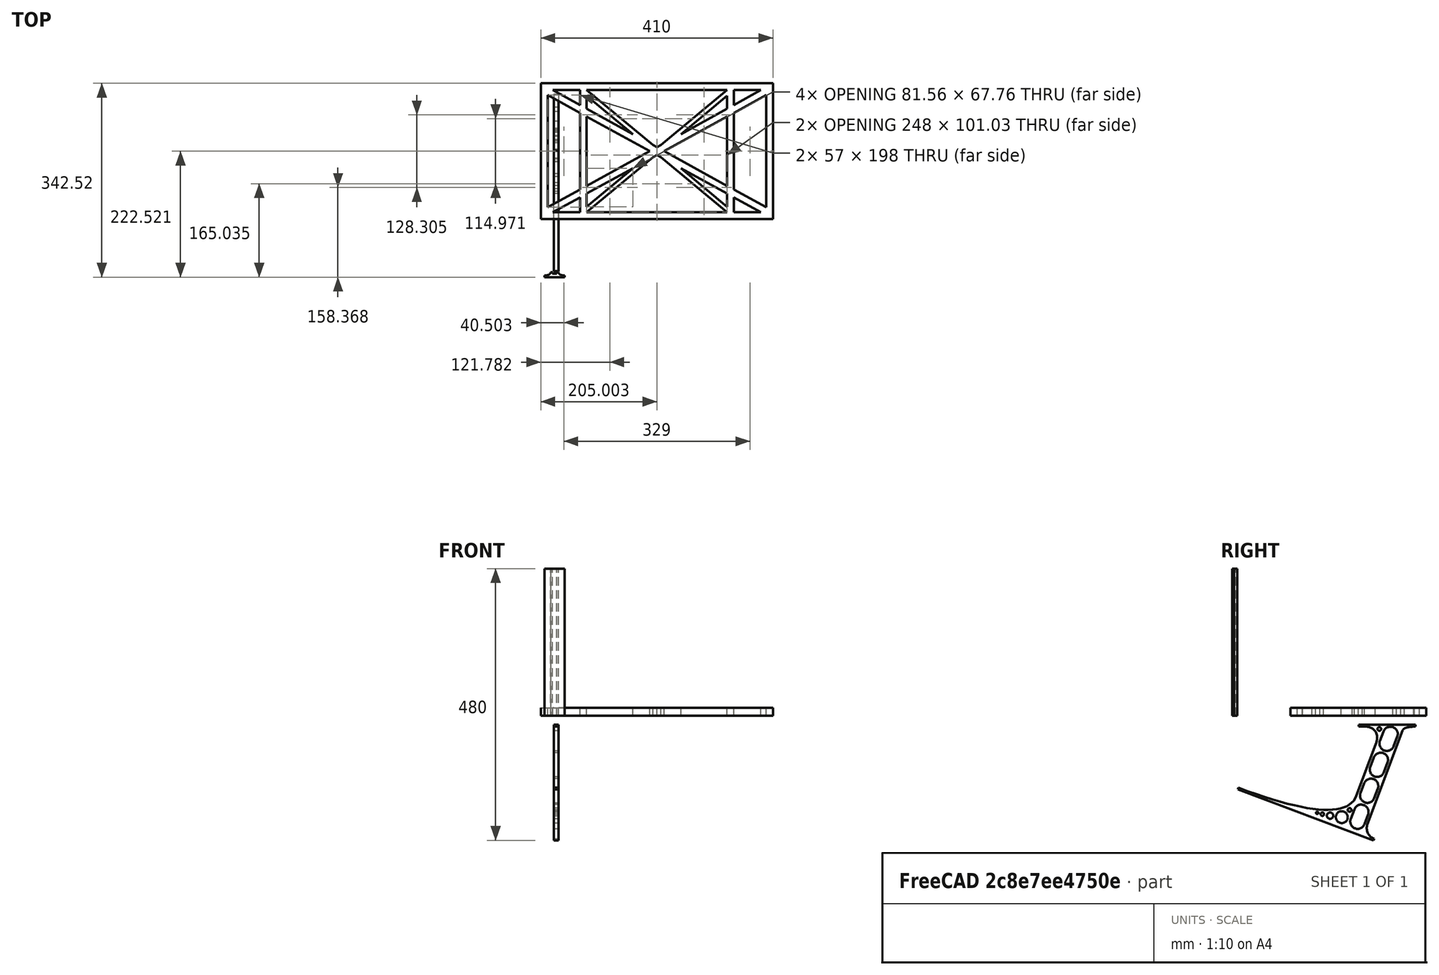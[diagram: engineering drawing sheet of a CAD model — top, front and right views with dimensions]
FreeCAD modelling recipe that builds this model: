
FCSTD DOCUMENT  (FreeCAD 0.19R0.19.2)
Label: laptopStand057
License: All rights reserved
LicenseURL: http://en.wikipedia.org/wiki/All_rights_reserved
objects: Sketcher::SketchObject×3, Part::Extrusion×3
note: 6 computed .brp shape members not serialized (recipe doc carries the construction recipe); baked Part::Feature solids carry a one-line shape summary decoded from their .brp

FEATURE [Sketcher::SketchObject] Sketch
  FullyConstrained = false
  sketch-geometry (106):
    g0: LineSegment StartX=-22.9272 StartY=136.221 StartZ=0 EndX=387.073 EndY=136.221 EndZ=0
    g1: LineSegment StartX=-22.9272 StartY=-103.779 StartZ=0 EndX=387.073 EndY=-103.779 EndZ=0
    g2: LineSegment StartX=375.073 StartY=115.221 StartZ=0 EndX=318.073 EndY=83.9235 EndZ=0
    g3: LineSegment StartX=-10.9272 StartY=-82.7794 StartZ=0 EndX=46.0728 EndY=-51.4823 EndZ=0
    g4: LineSegment StartX=-1.92718 StartY=124.221 StartZ=0 EndX=46.0728 EndY=97.8651 EndZ=0
    g5: LineSegment StartX=366.073 StartY=-91.7794 StartZ=0 EndX=318.073 EndY=-65.424 EndZ=0
    g6: LineSegment StartX=-10.9272 StartY=115.221 StartZ=0 EndX=-10.9272 EndY=-82.7794 EndZ=0
    g7: LineSegment StartX=375.073 StartY=-82.7794 StartZ=0 EndX=375.073 EndY=115.221 EndZ=0
    g8: LineSegment StartX=-1.92719 StartY=-91.7794 StartZ=0 EndX=46.0728 EndY=-91.7794 EndZ=0
    g9: LineSegment StartX=318.073 StartY=124.221 StartZ=0 EndX=366.073 EndY=124.221 EndZ=0
    g10: LineSegment StartX=306.073 StartY=-81.8102 StartZ=0 EndX=224.513 EndY=-14.0532 EndZ=0
    g11: LineSegment StartX=58.0728 StartY=114.251 StartZ=0 EndX=139.632 EndY=46.4944 EndZ=0
    g12: LineSegment StartX=306.073 StartY=124.221 StartZ=0 EndX=189.124 EndY=27.0628 EndZ=0
    g13: LineSegment StartX=58.0728 StartY=-91.7794 StartZ=0 EndX=175.022 EndY=5.37834 EndZ=0
    g14: LineSegment StartX=46.0728 StartY=124.221 StartZ=0 EndX=46.0728 EndY=97.8651 EndZ=0
    g15: LineSegment StartX=58.0728 StartY=-81.8102 StartZ=0 EndX=58.0728 EndY=-58.8351 EndZ=0
    g16: LineSegment StartX=318.073 StartY=124.221 StartZ=0 EndX=318.073 EndY=97.8651 EndZ=0
    g17: LineSegment StartX=306.073 StartY=114.251 StartZ=0 EndX=306.073 EndY=91.2763 EndZ=0
    g18: LineSegment StartX=224.513 StartY=46.4944 StartZ=0 EndX=306.073 EndY=114.251 EndZ=0
    g19: LineSegment StartX=175.022 StartY=27.0628 StartZ=0 EndX=58.0728 EndY=124.221 EndZ=0
    g20: LineSegment StartX=169.377 StartY=16.2206 StartZ=0 EndX=58.0728 EndY=77.3346 EndZ=0
    g21: LineSegment StartX=139.632 StartY=-14.0532 StartZ=0 EndX=58.0728 EndY=-81.8102 EndZ=0
    g22: LineSegment StartX=194.768 StartY=16.2206 StartZ=0 EndX=306.073 EndY=-44.8935 EndZ=0
    g23: LineSegment StartX=224.513 StartY=46.4944 StartZ=0 EndX=306.073 EndY=91.2763 EndZ=0
    g24: LineSegment StartX=139.632 StartY=-14.0532 StartZ=0 EndX=58.0728 EndY=-58.8351 EndZ=0
    g25: LineSegment StartX=189.124 StartY=5.37834 StartZ=0 EndX=306.073 EndY=-91.7794 EndZ=0
    g26: LineSegment StartX=306.073 StartY=77.3346 StartZ=0 EndX=306.073 EndY=-44.8935 EndZ=0
    g27: LineSegment StartX=318.073 StartY=83.9235 StartZ=0 EndX=318.073 EndY=-51.4823 EndZ=0
    g28: LineSegment StartX=318.073 StartY=97.8651 StartZ=0 EndX=366.073 EndY=124.221 EndZ=0
    g29: LineSegment StartX=306.073 StartY=77.3346 StartZ=0 EndX=194.768 EndY=16.2206 EndZ=0
    g30: LineSegment StartX=306.073 StartY=-58.8351 StartZ=0 EndX=224.513 EndY=-14.0532 EndZ=0
    g31: LineSegment StartX=306.073 StartY=-58.8351 StartZ=0 EndX=306.073 EndY=-81.8102 EndZ=0
    g32: LineSegment StartX=318.073 StartY=-51.4823 StartZ=0 EndX=375.073 EndY=-82.7794 EndZ=0
    g33: LineSegment StartX=318.073 StartY=-65.424 StartZ=0 EndX=318.073 EndY=-91.7794 EndZ=0
    g34: LineSegment StartX=318.073 StartY=-91.7794 StartZ=0 EndX=366.073 EndY=-91.7794 EndZ=0
    g35: LineSegment StartX=58.0728 StartY=-44.8935 StartZ=0 EndX=58.0728 EndY=77.3346 EndZ=0
    g36: LineSegment StartX=46.0728 StartY=-65.424 StartZ=0 EndX=-1.92719 EndY=-91.7794 EndZ=0
    g37: LineSegment StartX=46.0728 StartY=-65.424 StartZ=0 EndX=46.0728 EndY=-91.7794 EndZ=0
    g38: LineSegment StartX=58.0728 StartY=-44.8935 StartZ=0 EndX=169.377 EndY=16.2206 EndZ=0
    g39: LineSegment StartX=58.0728 StartY=91.2763 StartZ=0 EndX=58.0728 EndY=114.251 EndZ=0
    g40: LineSegment StartX=46.0728 StartY=83.9235 StartZ=0 EndX=46.0728 EndY=-51.4823 EndZ=0
    g41: LineSegment StartX=46.0728 StartY=124.221 StartZ=0 EndX=-1.92719 EndY=124.221 EndZ=0
    g42: LineSegment StartX=58.0728 StartY=91.2763 StartZ=0 EndX=139.632 EndY=46.4944 EndZ=0
    g43: LineSegment StartX=46.0728 StartY=83.9235 StartZ=0 EndX=-10.9272 EndY=115.221 EndZ=0
    g44: LineSegment StartX=-22.9272 StartY=136.221 StartZ=0 EndX=-42.9272 EndY=136.221 EndZ=0
    g45: LineSegment StartX=387.073 StartY=136.221 StartZ=0 EndX=407.073 EndY=136.221 EndZ=0
    g46: LineSegment StartX=-42.9272 StartY=136.221 StartZ=0 EndX=-42.9272 EndY=-103.779 EndZ=0
    g47: LineSegment StartX=-22.9272 StartY=-103.779 StartZ=0 EndX=-42.9272 EndY=-103.779 EndZ=0
    g48: LineSegment StartX=407.073 StartY=136.221 StartZ=0 EndX=407.073 EndY=-103.779 EndZ=0
    g49: LineSegment StartX=387.073 StartY=-103.779 StartZ=0 EndX=407.073 EndY=-103.779 EndZ=0
    g50: LineSegment StartX=179.022 StartY=27.0628 StartZ=0 EndX=179.022 EndY=124.221 EndZ=0
    g51: LineSegment StartX=185.124 StartY=27.0628 StartZ=0 EndX=185.124 EndY=124.221 EndZ=0
    g52: ArcOfCircle CenterX=-26.9272 CenterY=22.1087 CenterZ=0 NormalX=0 NormalY=0 NormalZ=1 AngleXU=0 Radius=8 StartAngle=1e-16 EndAngle=3.14159
    g53: ArcOfCircle CenterX=-26.9272 CenterY=-83.7794 CenterZ=0 NormalX=0 NormalY=0 NormalZ=1 AngleXU=0 Radius=8 StartAngle=3.14159 EndAngle=6.28319
    g54: LineSegment StartX=-34.9272 StartY=22.1087 StartZ=0 EndX=-34.9272 EndY=-83.7794 EndZ=0
    g55: LineSegment StartX=-18.9272 StartY=22.1087 StartZ=0 EndX=-18.9272 EndY=-83.7794 EndZ=0
    g56: LineSegment StartX=185.124 StartY=-91.7794 StartZ=0 EndX=306.073 EndY=-91.7794 EndZ=0
    g57: LineSegment StartX=179.022 StartY=-91.7794 StartZ=0 EndX=58.0728 EndY=-91.7794 EndZ=0
    g58: LineSegment StartX=306.073 StartY=124.221 StartZ=0 EndX=185.124 EndY=124.221 EndZ=0
    g59: LineSegment StartX=179.022 StartY=124.221 StartZ=0 EndX=58.0728 EndY=124.221 EndZ=0
    g60: ArcOfCircle CenterX=391.073 CenterY=22.1087 CenterZ=0 NormalX=0 NormalY=0 NormalZ=1 AngleXU=0 Radius=8 StartAngle=-4.4e-15 EndAngle=3.14159
    g61: LineSegment StartX=399.073 StartY=22.1087 StartZ=0 EndX=399.073 EndY=-83.7794 EndZ=0
    g62: LineSegment StartX=383.073 StartY=22.1087 StartZ=0 EndX=383.073 EndY=-83.7794 EndZ=0
    g63: ArcOfCircle CenterX=391.073 CenterY=-83.7794 CenterZ=0 NormalX=0 NormalY=0 NormalZ=1 AngleXU=0 Radius=8 StartAngle=3.14159 EndAngle=6.28319
    g64: Circle CenterX=175.022 CenterY=27.0628 CenterZ=0 NormalX=0 NormalY=0 NormalZ=1 AngleXU=0 Radius=1
    g65: Circle CenterX=179.022 CenterY=24.8665 CenterZ=0 NormalX=0 NormalY=0 NormalZ=1 AngleXU=0 Radius=1
    g66: Circle CenterX=179.022 CenterY=27.0628 CenterZ=0 NormalX=0 NormalY=0 NormalZ=1 AngleXU=0 Radius=1
    g67: BSplineCurve PolesCount=3 KnotsCount=2 Degree=2 IsPeriodic=0
    g68: GeomPoint X=175.022 Y=27.0628 Z=0
    g69: GeomPoint X=179.022 Y=27.0628 Z=0
    g70: Circle CenterX=189.124 CenterY=27.0628 CenterZ=0 NormalX=0 NormalY=0 NormalZ=1 AngleXU=0 Radius=1
    g71: Circle CenterX=185.124 CenterY=24.8665 CenterZ=0 NormalX=0 NormalY=0 NormalZ=1 AngleXU=0 Radius=1
    g72: Circle CenterX=185.124 CenterY=27.0628 CenterZ=0 NormalX=0 NormalY=0 NormalZ=1 AngleXU=0 Radius=1
    g73: BSplineCurve PolesCount=3 KnotsCount=2 Degree=2 IsPeriodic=0
    g74: GeomPoint X=189.124 Y=27.0628 Z=0
    g75: GeomPoint X=185.124 Y=27.0628 Z=0
    g76: Circle CenterX=175.022 CenterY=5.37834 CenterZ=0 NormalX=0 NormalY=0 NormalZ=1 AngleXU=0 Radius=1
    g77: Circle CenterX=179.022 CenterY=7.57463 CenterZ=0 NormalX=0 NormalY=0 NormalZ=1 AngleXU=0 Radius=1
    g78: Circle CenterX=179.022 CenterY=5.34704 CenterZ=0 NormalX=0 NormalY=0 NormalZ=1 AngleXU=0 Radius=1
    g79: BSplineCurve PolesCount=3 KnotsCount=2 Degree=2 IsPeriodic=0
    g80: GeomPoint X=175.022 Y=5.37834 Z=0
    g81: GeomPoint X=179.022 Y=5.34704 Z=0
    g82: Circle CenterX=189.124 CenterY=5.37834 CenterZ=0 NormalX=0 NormalY=0 NormalZ=1 AngleXU=0 Radius=1
    g83: Circle CenterX=185.124 CenterY=7.57463 CenterZ=0 NormalX=0 NormalY=0 NormalZ=1 AngleXU=0 Radius=1
    g84: Circle CenterX=185.124 CenterY=5.34704 CenterZ=0 NormalX=0 NormalY=0 NormalZ=1 AngleXU=0 Radius=1
    g85: BSplineCurve PolesCount=3 KnotsCount=2 Degree=2 IsPeriodic=0
    g86: GeomPoint X=189.124 Y=5.37834 Z=0
    g87: GeomPoint X=185.124 Y=5.34704 Z=0
    g88: LineSegment StartX=179.022 StartY=5.34704 StartZ=0 EndX=179.022 EndY=-91.7794 EndZ=0
    g89: LineSegment StartX=185.124 StartY=-91.7794 StartZ=0 EndX=185.124 EndY=5.34704 EndZ=0
    g90: LineSegment StartX=169.377 StartY=16.2206 StartZ=0 EndX=165.871 EndY=14.2954 EndZ=0
    g91: LineSegment StartX=198.275 StartY=18.1458 StartZ=0 EndX=194.768 EndY=16.2206 EndZ=0
    g92: LineSegment StartX=169.377 StartY=16.2206 StartZ=0 EndX=165.871 EndY=18.1458 EndZ=0
    g93: LineSegment StartX=198.275 StartY=14.2954 StartZ=0 EndX=194.768 EndY=16.2206 EndZ=0
    g94: Circle CenterX=165.871 CenterY=18.1458 CenterZ=0 NormalX=0 NormalY=0 NormalZ=1 AngleXU=0 Radius=1
    g95: Circle CenterX=169.377 CenterY=16.2206 CenterZ=0 NormalX=0 NormalY=0 NormalZ=1 AngleXU=0 Radius=1
    g96: Circle CenterX=165.871 CenterY=14.2954 CenterZ=0 NormalX=0 NormalY=0 NormalZ=1 AngleXU=0 Radius=1
    g97: BSplineCurve PolesCount=3 KnotsCount=2 Degree=2 IsPeriodic=0
    g98: GeomPoint X=165.871 Y=18.1458 Z=0
    g99: GeomPoint X=165.871 Y=14.2954 Z=0
    g100: Circle CenterX=198.275 CenterY=18.1458 CenterZ=0 NormalX=0 NormalY=0 NormalZ=1 AngleXU=0 Radius=1
    g101: Circle CenterX=194.768 CenterY=16.2206 CenterZ=0 NormalX=0 NormalY=0 NormalZ=1 AngleXU=0 Radius=1
    g102: Circle CenterX=198.275 CenterY=14.2954 CenterZ=0 NormalX=0 NormalY=0 NormalZ=1 AngleXU=0 Radius=1
    g103: BSplineCurve PolesCount=3 KnotsCount=2 Degree=2 IsPeriodic=0
    g104: GeomPoint X=198.275 Y=18.1458 Z=0
    g105: GeomPoint X=198.275 Y=14.2954 Z=0
  constraints (210):
    c: Horizontal(g0)
    c: Distance(g0) = 410
    c: Horizontal(g1)
    c: Block(g0)
    c: Horizontal(g8)
    c: Horizontal(g9)
    c: Tangent(g5,g20)
    c: PointOnObject(g20,g3)
    c: PointOnObject(g22,g2)
    c: Coincident(g42,g11)
    c: Coincident(g18,g23)
    c: Coincident(g24,g21)
    c: Coincident(g30,g10)
    c: Coincident(g18,g17)
    c: Tangent(g17,g26)
    c: Tangent(g16,g27)
    c: Coincident(g23,g17)
    c: Tangent(g23,g28)
    c: Coincident(g2,g27)
    c: Coincident(g29,g26)
    c: Tangent(g2,g29)
    c: Coincident(g31,g10)
    c: Tangent(g5,g30)
    c: Tangent(g26,g31)
    c: Coincident(g22,g26)
    c: Tangent(g22,g32)
    c: Coincident(g27,g32)
    c: Coincident(g33,g5)
    c: Tangent(g27,g33)
    c: Coincident(g21,g15)
    c: Tangent(g15,g35)
    c: Coincident(g24,g15)
    c: Tangent(g24,g36)
    c: Coincident(g37,g36)
    c: Tangent(g14,g37)
    c: Coincident(g3,g40)
    c: Coincident(g38,g35)
    c: Tangent(g35,g39)
    c: Tangent(g14,g40)
    c: Coincident(g11,g39)
    c: Coincident(g4,g14)
    c: Coincident(g42,g39)
    c: Tangent(g4,g42)
    c: Coincident(g20,g35)
    c: Coincident(g43,g40)
    c: Tangent(g20,g43)
    c: Block(g19)
    c: Block(g12)
    c: Block(g16)
    c: Block(g28)
    c: Block(g2)
    c: Block(g32)
    c: Block(g7)
    c: Block(g30)
    c: Block(g31)
    c: Block(g5)
    c: Block(g33)
    c: Block(g18)
    c: Block(g25)
    c: Block(g13)
    c: Block(g24)
    c: Block(g21)
    c: Block(g37)
    c: Block(g36)
    c: Block(g3)
    c: Block(g6)
    c: Block(g43)
    c: Block(g4)
    c: Block(g14)
    c: Block(g11)
    c: Block(g39)
    c: Block(g29)
    c: Block(g26)
    c: Block(g20)
    c: Block(g38)
    c: Block(g41)
    c: Block(g9)
    c: Block(g34)
    c: Block(g8)
    c: Horizontal(g44)
    c: Distance(g44) = 20
    c: Coincident(g45,g0)
    c: Horizontal(g45)
    c: Distance(g45) = 20
    c: Coincident(g46,g44)
    c: Vertical(g46)
    c: Horizontal(g47)
    c: Coincident(g47,g46)
    c: Coincident(g48,g45)
    c: Vertical(g48)
    c: Coincident(g49,g1)
    c: Horizontal(g49)
    c: Coincident(g49,g48)
    c: Block(g48)
    c: Block(g47)
    c: Block(g46)
    c: Block(g1)
    c: Vertical(g50)
    c: Vertical(g51)
    c: Block(g50)
    c: Block(g51)
    c: Tangent(g52,g55) = 1.5708
    c: Tangent(g52,g54) = -1.5708
    c: Tangent(g54,g53) = -1.5708
    c: Tangent(g55,g53) = 1.5708
    c: Vertical(g54)
    c: Equal(g52,g53)
    c: Block(g55)
    c: Block(g54)
    c: Coincident(g56,g25)
    c: Horizontal(g56)
    c: Coincident(g57,g13)
    c: Horizontal(g57)
    c: Coincident(g58,g12)
    c: Coincident(g58,g51)
    c: Horizontal(g58)
    c: Coincident(g59,g50)
    c: Coincident(g59,g19)
    c: Horizontal(g59)
    c: Distance(g49) = 20
    c: Distance(g1) = 410
    c: Tangent(g60,g61) = 1.5708
    c: Tangent(g61,g63) = 1.5708
    c: Equal(g60,g63)
    c: Coincident(g62,g60)
    c: Coincident(g62,g63)
    c: Block(g61)
    c: Block(g62)
    c: Block(g22)
    c: Coincident(g67,g19)
    c: Weight(g64) = 1
    c: Equal(g64,g65)
    c: Equal(g64,g66)
    c: Coincident(g67,g50)
    c: InternalAlignment(g64,g67)
    c: InternalAlignment(g65,g67)
    c: InternalAlignment(g66,g67)
    c: InternalAlignment(g68,g67)
    c: InternalAlignment(g69,g67)
    c: Coincident(g73,g12)
    c: Weight(g70) = 1
    c: Equal(g70,g71)
    c: Equal(g70,g72)
    c: Coincident(g73,g51)
    c: InternalAlignment(g70,g73)
    c: InternalAlignment(g71,g73)
    c: InternalAlignment(g72,g73)
    c: InternalAlignment(g74,g73)
    c: InternalAlignment(g75,g73)
    c: Block(g73)
    c: Block(g67)
    c: Coincident(g79,g13)
    c: Weight(g76) = 1
    c: Equal(g76,g77)
    c: Equal(g76,g78)
    c: InternalAlignment(g76,g79)
    c: InternalAlignment(g77,g79)
    c: InternalAlignment(g78,g79)
    c: InternalAlignment(g80,g79)
    c: InternalAlignment(g81,g79)
    c: Weight(g82) = 1
    c: Equal(g82,g83)
    c: Equal(g82,g84)
    c: InternalAlignment(g82,g85)
    c: InternalAlignment(g83,g85)
    c: InternalAlignment(g84,g85)
    c: InternalAlignment(g86,g85)
    c: InternalAlignment(g87,g85)
    c: Block(g85)
    c: Block(g79)
    c: Coincident(g88,g79)
    c: Coincident(g88,g57)
    c: Vertical(g88)
    c: Coincident(g89,g56)
    c: Coincident(g89,g85)
    c: Vertical(g89)
    c: Distance(g90) = 4
    c: Parallel(g38,g90)
    c: Equal(g90,g91) = 4
    c: Distance(g92) = 4
    c: Equal(g92,g93) = 4
    c: Coincident(g90,g20)
    c: Coincident(g92,g20)
    c: Parallel(g92,g20)
    c: Coincident(g93,g22)
    c: Parallel(g22,g93)
    c: Coincident(g91,g22)
    c: Parallel(g29,g91)
    c: Coincident(g97,g92)
    c: Weight(g94) = 1
    c: Equal(g94,g95)
    c: Coincident(g95,g20)
    c: Equal(g94,g96)
    c: Coincident(g97,g90)
    c: InternalAlignment(g94,g97)
    c: InternalAlignment(g95,g97)
    c: InternalAlignment(g96,g97)
    c: InternalAlignment(g98,g97)
    c: InternalAlignment(g99,g97)
    c: Coincident(g103,g91)
    c: Weight(g100) = 1
    c: Equal(g100,g101)
    c: Coincident(g101,g22)
    c: Equal(g100,g102)
    c: Coincident(g103,g93)
    c: InternalAlignment(g100,g103)
    c: InternalAlignment(g101,g103)
    c: InternalAlignment(g102,g103)
    c: InternalAlignment(g104,g103)
    c: InternalAlignment(g105,g103)
FEATURE [Sketcher::SketchObject] Sketch001
  FullyConstrained = true
  MapMode = 4
  Placement = pos=(0,0,0) rot=(0.57735,0.57735,0.57735;2.0944rad)
  Support = -> [Sketch]
  sketch-geometry (46):
    g0: BSplineCurve PolesCount=3 KnotsCount=2 Degree=2 IsPeriodic=0
    g1: ArcOfCircle CenterX=73.122 CenterY=-32.2909 CenterZ=0 NormalX=0 NormalY=0 NormalZ=1 AngleXU=0 Radius=13 StartAngle=5.92268 EndAngle=9.06428
    g2: ArcOfCircle CenterX=66.7816 CenterY=-49.1439 CenterZ=0 NormalX=0 NormalY=0 NormalZ=1 AngleXU=0 Radius=13 StartAngle=2.78068 EndAngle=5.92131
    g3: ArcOfCircle CenterX=55.9263 CenterY=-78.1807 CenterZ=0 NormalX=0 NormalY=0 NormalZ=1 AngleXU=0 Radius=13 StartAngle=5.92268 EndAngle=9.06428
    g4: ArcOfCircle CenterX=49.5884 CenterY=-95.0342 CenterZ=0 NormalX=0 NormalY=0 NormalZ=1 AngleXU=0 Radius=13 StartAngle=2.78068 EndAngle=5.92131
    g5: ArcOfCircle CenterX=38.7206 CenterY=-124.067 CenterZ=0 NormalX=0 NormalY=0 NormalZ=1 AngleXU=0 Radius=13 StartAngle=5.92268 EndAngle=9.06428
    g6: ArcOfCircle CenterX=32.3875 CenterY=-140.92 CenterZ=0 NormalX=0 NormalY=0 NormalZ=1 AngleXU=0 Radius=13 StartAngle=2.78068 EndAngle=5.92131
    g7: ArcOfCircle CenterX=21.4715 CenterY=-169.934 CenterZ=0 NormalX=0 NormalY=0 NormalZ=1 AngleXU=0 Radius=13 StartAngle=5.92268 EndAngle=9.06428
    g8: ArcOfCircle CenterX=15.1336 CenterY=-186.787 CenterZ=0 NormalX=0 NormalY=0 NormalZ=1 AngleXU=0 Radius=13 StartAngle=2.78068 EndAngle=5.92131
    g9-g12: Circle x4 (B-spline internal-alignment scaffolding for g13; pole/knot coordinates omitted)
    g13: BSplineCurve PolesCount=4 KnotsCount=2 Degree=3 IsPeriodic=0
    g14: GeomPoint X=28.8094 Y=-19.0875 Z=0
    g15: GeomPoint X=47.0443 Y=-50.4712 Z=0
    g16: Circle CenterX=53.5586 CenterY=-23.2695 CenterZ=0 NormalX=0 NormalY=0 NormalZ=1 AngleXU=0 Radius=3.24518
    g17: Circle CenterX=-195.441 CenterY=-127.082 CenterZ=0 NormalX=0 NormalY=0 NormalZ=1 AngleXU=0 Radius=1
    g18: Circle CenterX=-8.24091 CenterY=-197.481 CenterZ=0 NormalX=0 NormalY=0 NormalZ=1 AngleXU=0 Radius=1
    g19: Circle CenterX=12.8789 CenterY=-141.321 CenterZ=0 NormalX=0 NormalY=0 NormalZ=1 AngleXU=0 Radius=1
    g20: BSplineCurve PolesCount=3 KnotsCount=2 Degree=2 IsPeriodic=0
    g21: GeomPoint X=-195.441 Y=-127.082 Z=0
    g22: GeomPoint X=12.8789 Y=-141.321 Z=0
    g23: Circle CenterX=-12.8016 CenterY=-179.036 CenterZ=0 NormalX=0 NormalY=0 NormalZ=1 AngleXU=0 Radius=10.5072
    g24: Circle CenterX=0.933922 CenterY=-166.43 CenterZ=0 NormalX=0 NormalY=0 NormalZ=1 AngleXU=0 Radius=3.26661
    g25: Circle CenterX=-33.5518 CenterY=-176.44 CenterZ=0 NormalX=0 NormalY=0 NormalZ=1 AngleXU=0 Radius=5.64388
    g26: Circle CenterX=-47.2366 CenterY=-173.859 CenterZ=0 NormalX=0 NormalY=0 NormalZ=1 AngleXU=0 Radius=3.01653
    g27: Circle CenterX=-56.2595 CenterY=-171.456 CenterZ=0 NormalX=0 NormalY=0 NormalZ=1 AngleXU=0 Radius=2.12826
    g28: ArcOfCircle CenterX=51.2151 CenterY=-198.473 CenterZ=0 NormalX=0 NormalY=0 NormalZ=1 AngleXU=0 Radius=20 StartAngle=2.78189 EndAngle=4.35269
    g29: LineSegment StartX=32.4951 StartY=-191.433 StartZ=0 EndX=94.6577 EndY=-26.1351 EndZ=0
    g30: LineSegment StartX=43.1192 StartY=-220.001 StartZ=0 EndX=-196.497 EndY=-129.89 EndZ=0
    g31: LineSegment StartX=43.1192 StartY=-220.001 StartZ=0 EndX=44.1752 EndY=-217.193 EndZ=0
    g32: LineSegment StartX=117.223 StartY=-19.0875 StartZ=0 EndX=117.223 EndY=-16.0875 EndZ=0
    g33: LineSegment StartX=117.223 StartY=-16.0875 StartZ=0 EndX=17.2232 EndY=-16.0875 EndZ=0
    g34: LineSegment StartX=17.2232 StartY=-16.0875 StartZ=0 EndX=17.2232 EndY=-19.0875 EndZ=0
    g35: LineSegment StartX=28.8094 StartY=-19.0875 StartZ=0 EndX=17.2232 EndY=-19.0875 EndZ=0
    g36: LineSegment StartX=47.0443 StartY=-50.4712 StartZ=0 EndX=12.8789 EndY=-141.321 EndZ=0
    g37: LineSegment StartX=-195.441 StartY=-127.082 StartZ=0 EndX=-196.497 EndY=-129.89 EndZ=0
    g38: LineSegment StartX=85.2864 StartY=-36.8765 StartZ=0 EndX=78.9396 EndY=-53.7463 EndZ=0
    g39: LineSegment StartX=60.9577 StartY=-27.7052 StartZ=0 EndX=54.6191 EndY=-44.5532 EndZ=0
    g40: LineSegment StartX=68.0907 StartY=-82.7664 StartZ=0 EndX=61.7465 EndY=-99.6365 EndZ=0
    g41: LineSegment StartX=43.7619 StartY=-73.595 StartZ=0 EndX=37.426 EndY=-90.4435 EndZ=0
    g42: LineSegment StartX=50.885 StartY=-128.652 StartZ=0 EndX=44.5456 EndY=-145.522 EndZ=0
    g43: LineSegment StartX=26.5562 StartY=-119.481 StartZ=0 EndX=20.2251 EndY=-136.329 EndZ=0
    g44: LineSegment StartX=9.3071 StartY=-165.349 StartZ=0 EndX=2.97115 EndY=-182.197 EndZ=0
    g45: LineSegment StartX=33.6358 StartY=-174.52 StartZ=0 EndX=27.2917 EndY=-191.39 EndZ=0
  constraints (70):
    c: Block(g0)
    c: Block(g1)
    c: Block(g2)
    c: Block(g4)
    c: Block(g3)
    c: Block(g6)
    c: Block(g5)
    c: Block(g8)
    c: Block(g7)
    c: Weight(g9) = 1
    c: Equal(g9,g10)
    c: Equal(g9,g11)
    c: Equal(g9,g12)
    c: InternalAlignment(g9-g12 -> g13) x4
    c: InternalAlignment(g14,g13)
    c: InternalAlignment(g15,g13)
    c: Block(g16)
    c: Weight(g17) = 1
    c: Equal(g17,g18)
    c: Equal(g17,g19)
    c: InternalAlignment(g17,g20)
    c: InternalAlignment(g18,g20)
    c: InternalAlignment(g19,g20)
    c: InternalAlignment(g21,g20)
    c: InternalAlignment(g22,g20)
    c: Block(g20)
    c: Block(g23)
    c: Block(g24)
    c: Block(g25)
    c: Block(g26)
    c: Block(g27)
    c: Block(g28)
    c: Coincident(g29,g28)
    c: Coincident(g29,g0)
    c: Block(g13)
    c: Coincident(g31,g30)
    c: Coincident(g31,g28)
    c: Block(g31)
    c: Coincident(g32,g0)
    c: Vertical(g32)
    c: Coincident(g33,g32)
    c: Horizontal(g33)
    c: Coincident(g34,g33)
    c: Vertical(g34)
    c: Block(g33)
    c: Coincident(g35,g13)
    c: Coincident(g35,g34)
    c: Horizontal(g35)
    c: Coincident(g36,g13)
    c: Coincident(g36,g20)
    c: Coincident(g37,g20)
    c: Coincident(g37,g30)
    c: Block(g30)
    c: Coincident(g38,g1)
    c: Coincident(g38,g2)
    c: Coincident(g39,g1)
    c: Coincident(g39,g2)
    c: Coincident(g40,g3)
    c: Coincident(g40,g4)
    c: Coincident(g41,g3)
    c: Coincident(g41,g4)
    c: Coincident(g42,g5)
    c: Coincident(g42,g6)
    c: Coincident(g43,g5)
    c: Coincident(g43,g6)
    c: Coincident(g44,g7)
    c: Coincident(g44,g8)
    c: Coincident(g45,g7)
    c: Coincident(g45,g8)
    c: Distance(g30) = 256
FEATURE [Part::Extrusion] Extrude002
  Base = -> Sketch001
  Dir = (1,0,0)
  DirMode = 2
  FaceMakerClass = Part::FaceMakerBullseye
  LengthFwd = 8
  LengthRev = 0
  Solid = true
  Symmetric = false
FEATURE [Sketcher::SketchObject] Sketch002
  FullyConstrained = true
  sketch-geometry (20):
    g0: LineSegment StartX=-2.77179 StartY=-200.304 StartZ=0 EndX=5.22821 EndY=-200.304 EndZ=0
    g1: LineSegment StartX=5.22821 StartY=-200.304 StartZ=0 EndX=5.22821 EndY=-197.304 EndZ=0
    g2: LineSegment StartX=-2.77179 StartY=-200.304 StartZ=0 EndX=-2.77179 EndY=-197.304 EndZ=0
    g3: LineSegment StartX=5.22821 StartY=-197.304 StartZ=0 EndX=8.22821 EndY=-197.304 EndZ=0
    g4: LineSegment StartX=-2.77179 StartY=-197.304 StartZ=0 EndX=-5.77179 EndY=-197.304 EndZ=0
    g5: LineSegment StartX=19.2282 StartY=-203.304 StartZ=0 EndX=19.2282 EndY=-206.304 EndZ=0
    g6: LineSegment StartX=-16.7718 StartY=-203.304 StartZ=0 EndX=-16.7718 EndY=-206.304 EndZ=0
    g7: LineSegment StartX=-16.7718 StartY=-206.304 StartZ=0 EndX=19.2282 EndY=-206.304 EndZ=0
    g8: Circle CenterX=-16.7718 CenterY=-203.304 CenterZ=0 NormalX=0 NormalY=0 NormalZ=1 AngleXU=0 Radius=1
    g9: Circle CenterX=-5.77179 CenterY=-203.304 CenterZ=0 NormalX=0 NormalY=0 NormalZ=1 AngleXU=0 Radius=1
    g10: Circle CenterX=-5.77179 CenterY=-197.304 CenterZ=0 NormalX=0 NormalY=0 NormalZ=1 AngleXU=0 Radius=1
    g11: BSplineCurve PolesCount=3 KnotsCount=2 Degree=2 IsPeriodic=0
    g12: GeomPoint X=-16.7718 Y=-203.304 Z=0
    g13: GeomPoint X=-5.77179 Y=-197.304 Z=0
    g14: Circle CenterX=19.2282 CenterY=-203.304 CenterZ=0 NormalX=0 NormalY=0 NormalZ=1 AngleXU=0 Radius=1
    g15: Circle CenterX=8.22821 CenterY=-203.304 CenterZ=0 NormalX=0 NormalY=0 NormalZ=1 AngleXU=0 Radius=1
    g16: Circle CenterX=8.22821 CenterY=-197.304 CenterZ=0 NormalX=0 NormalY=0 NormalZ=1 AngleXU=0 Radius=1
    g17: BSplineCurve PolesCount=3 KnotsCount=2 Degree=2 IsPeriodic=0
    g18: GeomPoint X=19.2282 Y=-203.304 Z=0
    g19: GeomPoint X=8.22821 Y=-197.304 Z=0
  constraints (41):
    c: Horizontal(g0)
    c: Distance(g0) = 8
    c: Coincident(g1,g0)
    c: Vertical(g1)
    c: Distance(g1) = 3
    c: Coincident(g2,g0)
    c: Vertical(g2)
    c: Distance(g2) = 3
    c: Coincident(g3,g1)
    c: Horizontal(g3)
    c: Distance(g3) = 3
    c: Coincident(g4,g2)
    c: Horizontal(g4)
    c: Distance(g4) = 3
    c: Vertical(g5)
    c: Vertical(g6)
    c: Coincident(g7,g6)
    c: Coincident(g7,g5)
    c: Weight(g8) = 1
    c: Equal(g8,g9)
    c: Equal(g8,g10)
    c: Coincident(g11,g4)
    c: InternalAlignment(g8,g11)
    c: InternalAlignment(g9,g11)
    c: InternalAlignment(g10,g11)
    c: InternalAlignment(g12,g11)
    c: InternalAlignment(g13,g11)
    c: Coincident(g17,g5)
    c: Weight(g14) = 1
    c: Equal(g14,g15)
    c: Equal(g14,g16)
    c: Coincident(g17,g3)
    c: InternalAlignment(g14,g17)
    c: InternalAlignment(g15,g17)
    c: InternalAlignment(g16,g17)
    c: InternalAlignment(g18,g17)
    c: InternalAlignment(g19,g17)
    c: Block(g7)
    c: Block(g17)
    c: Block(g11)
    c: Block(g6)
FEATURE [Part::Extrusion] Extrude003
  Base = -> Sketch002
  Dir = (0,0,1)
  DirMode = 2
  FaceMakerClass = Part::FaceMakerBullseye
  LengthFwd = 260
  LengthRev = 0
  Solid = true
  Symmetric = false
FEATURE [Part::Extrusion] Extrude
  Base = -> Sketch
  Dir = (0,0,1)
  DirMode = 2
  FaceMakerClass = Part::FaceMakerBullseye
  LengthFwd = 14
  LengthRev = 0
  Solid = true
  Symmetric = false
